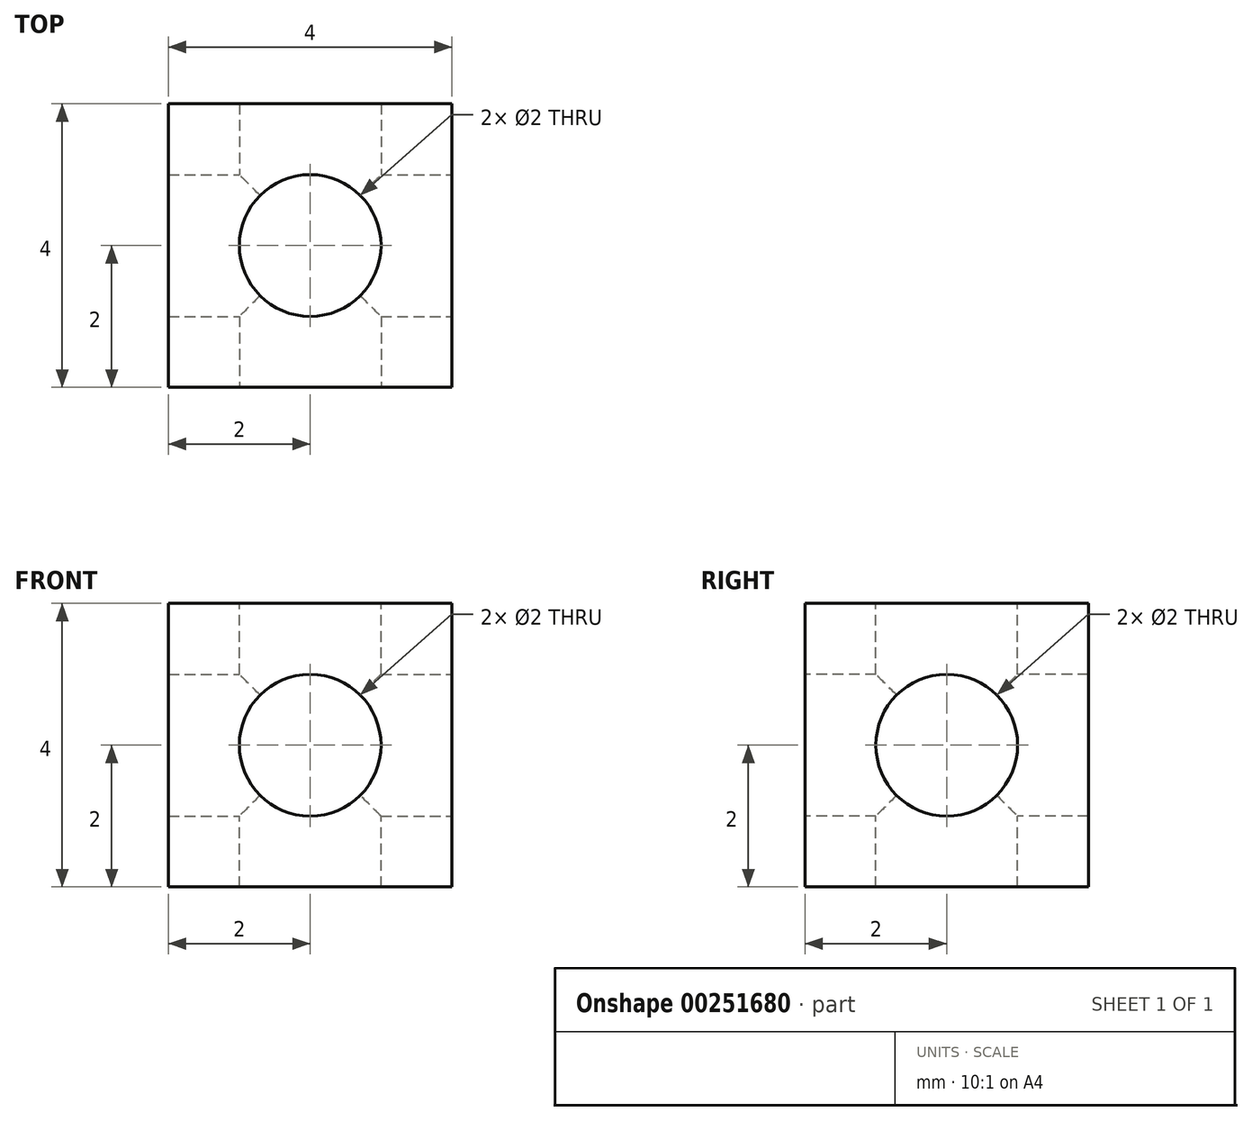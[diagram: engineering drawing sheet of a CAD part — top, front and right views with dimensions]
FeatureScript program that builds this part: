
annotation { "Feature Type Name" : "Feature", "Feature Type Description" : "" }
export const myFeature = defineFeature(function(context is Context, id is Id, definition is map)
    precondition{}
    {
        {
            var Q0;
            Q0=qCreatedBy(makeId("Top.planeOp"),FACE);
            var sketch = newSketch(context, id + "F0", { "sketchPlane" : qUnion([Q0])});
            skLineSegment(sketch, "E0.bottom", {"start": v(0, 0) * mm, "end": v(4, 0) * mm});
            skLineSegment(sketch, "E0.top", {"start": v(0, 4) * mm, "end": v(4, 4) * mm});
            skLineSegment(sketch, "E0.left", {"start": v(0, 0) * mm, "end": v(0, 4) * mm});
            skLineSegment(sketch, "E0.right", {"start": v(4, 0) * mm, "end": v(4, 4) * mm});
            skSolve(sketch);
        }
        {
            var Q0;
            Q0 = qSketchRegion(id + "F0", true);
            extrude(context, id + "F1", {"entities" : qUnion([Q0]), "depth" : 4 * mm});
        }
        {
            var Q0;
            Q0=makeQuery(id+"F1.opExtrude","CAP_FACE",FACE,{"disambiguationData":[OSD([sQuery(id+"F0.wireOp",EDGE,"E0.bottom"),sQuery(id+"F0.wireOp",EDGE,"E0.top"),sQuery(id+"F0.wireOp",EDGE,"E0.left"),sQuery(id+"F0.wireOp",EDGE,"E0.right")])],"isStart":false});
            var sketch = newSketch(context, id + "F2", { "sketchPlane" : qUnion([Q0])});
            skLineSegment(sketch, "E1", {"start": v(0, 4) * mm, "end": v(2, 4) * mm, "construction": true});
            skLineSegment(sketch, "E2", {"start": v(2, 4) * mm, "end": v(2, 2) * mm, "construction": true});
            skCircle(sketch, "E3", {"center": v(2, 2) * mm, "radius": 1 * mm});
            skSolve(sketch);
        }
        {
            var Q0;
            Q0 = qSketchRegion(id + "F2", true);
            extrude(context, id + "F3", {"entities" : qUnion([Q0]), "operationType" : NewBodyOperationType.REMOVE, "oppositeDirection" : true, "depth" : 25 * mm});
        }
        {
            var Q0;
            Q0=makeQuery(id+"F1.opExtrude","SWEPT_FACE",FACE,{"disambiguationData":[OSD([sQuery(id+"F0.wireOp",EDGE,"E0.bottom")])]});
            var sketch = newSketch(context, id + "F4", { "sketchPlane" : qUnion([Q0])});
            skLineSegment(sketch, "E4", {"start": v(0, 4) * mm, "end": v(2, 4) * mm, "construction": true});
            skLineSegment(sketch, "E5", {"start": v(2, 4) * mm, "end": v(2, 2) * mm, "construction": true});
            skCircle(sketch, "E6", {"center": v(2, 2) * mm, "radius": 1 * mm});
            skSolve(sketch);
        }
        {
            var Q0;
            Q0 = qSketchRegion(id + "F4", true);
            extrude(context, id + "F5", {"entities" : qUnion([Q0]), "operationType" : NewBodyOperationType.REMOVE, "oppositeDirection" : true, "depth" : 25 * mm});
        }
        {
            var Q0;
            Q0=makeQuery(id+"F1.opExtrude","SWEPT_FACE",FACE,{"disambiguationData":[OSD([sQuery(id+"F0.wireOp",EDGE,"E0.right")])]});
            var sketch = newSketch(context, id + "F6", { "sketchPlane" : qUnion([Q0])});
            skLineSegment(sketch, "E7", {"start": v(2, 4) * mm, "end": v(2, 2) * mm, "construction": true});
            skPoint(sketch, "E7.endSnap0", {"position": v(2, 4) * mm});
            skCircle(sketch, "E8", {"center": v(2, 2) * mm, "radius": 1 * mm});
            skSolve(sketch);
        }
        {
            var Q0;
            Q0 = qSketchRegion(id + "F6", true);
            extrude(context, id + "F7", {"entities" : qUnion([Q0]), "operationType" : NewBodyOperationType.REMOVE, "oppositeDirection" : true, "depth" : 25 * mm});
        }
    });
